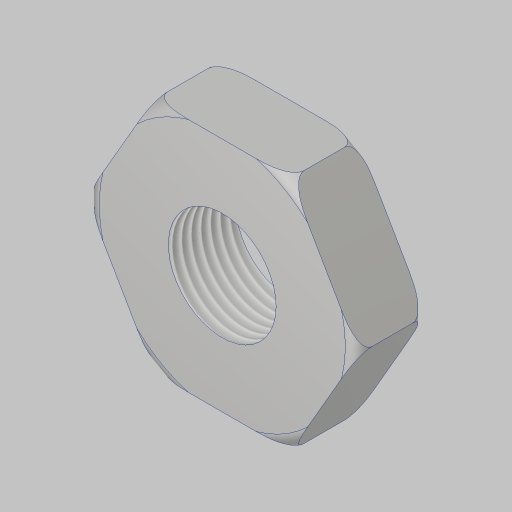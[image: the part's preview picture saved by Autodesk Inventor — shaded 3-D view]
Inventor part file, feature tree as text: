
AUTODESK INVENTOR PART (.ipt)
format: ipt  version: 2023.5 (Build 275446000, 446)  size: 242,688 bytes
history: native  units: in
note: dims shown in document units (in); Inventor stores cm internally (conversion verified against a paired STEP export)
features: sketch x3, extrude x1, hole x1, revolve x1, projected_geometry x1
ambient origin geometry x8: Origin, YZ Plane, XZ Plane, XY Plane, X Axis, Y Axis, Z Axis, Center Point
bodies: Solid1 (feature_tree)
feature tree (7):
  extrude  "Extrusion1"  Depth=0.5in TaperAngle=0.0deg
  hole  "Hole1"  [1 undecoded]
  revolve  "Revolution1"  [1 undecoded]
  sketch  "Sketch1"  dims[d1=1.75in d2=0.5in d3=0.0in]
  sketch  "Sketch2"  dims[d4=0.798in d5=1.75in d6=0.375in d7=0.25in d8=0.5635in d9=1.0in d10=0.8108in d11=0.1in]
  sketch  "Sketch3"  dims[d12=0.1in d13=0.1in d14=90.0deg]
  projected_geometry  "Project Cut Edges1"
note: 2 required parameter values undecoded (feature->parameter linkage not recoverable at this tier; creation-order binding heuristic only, values carry confidence <= 0.55)